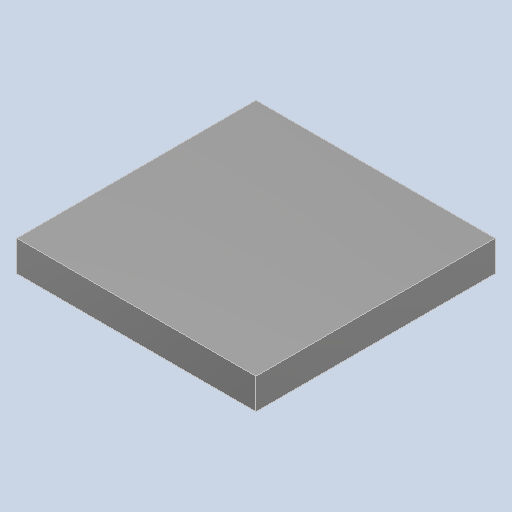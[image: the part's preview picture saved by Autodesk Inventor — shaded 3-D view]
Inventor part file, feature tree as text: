
AUTODESK INVENTOR PART (.ipt)
format: ipt  version: 2022 (Build 260153000, 153)  size: 82,944 bytes
history: imported  units: in
note: dims shown in document units (in); Inventor stores cm internally (conversion verified against a paired STEP export)
features: imported_body x1
ambient origin geometry x8: Origin, YZ Plane, XZ Plane, XY Plane, X Axis, Y Axis, Z Axis, Center Point
bodies: Solid1 (imported_parasolid)
feature tree (1):
  imported_body  NMx_Import_Brep_tag  [imported B-rep: ~6 faces, bbox_mm=[7.0, 0.9, 7.0]]
